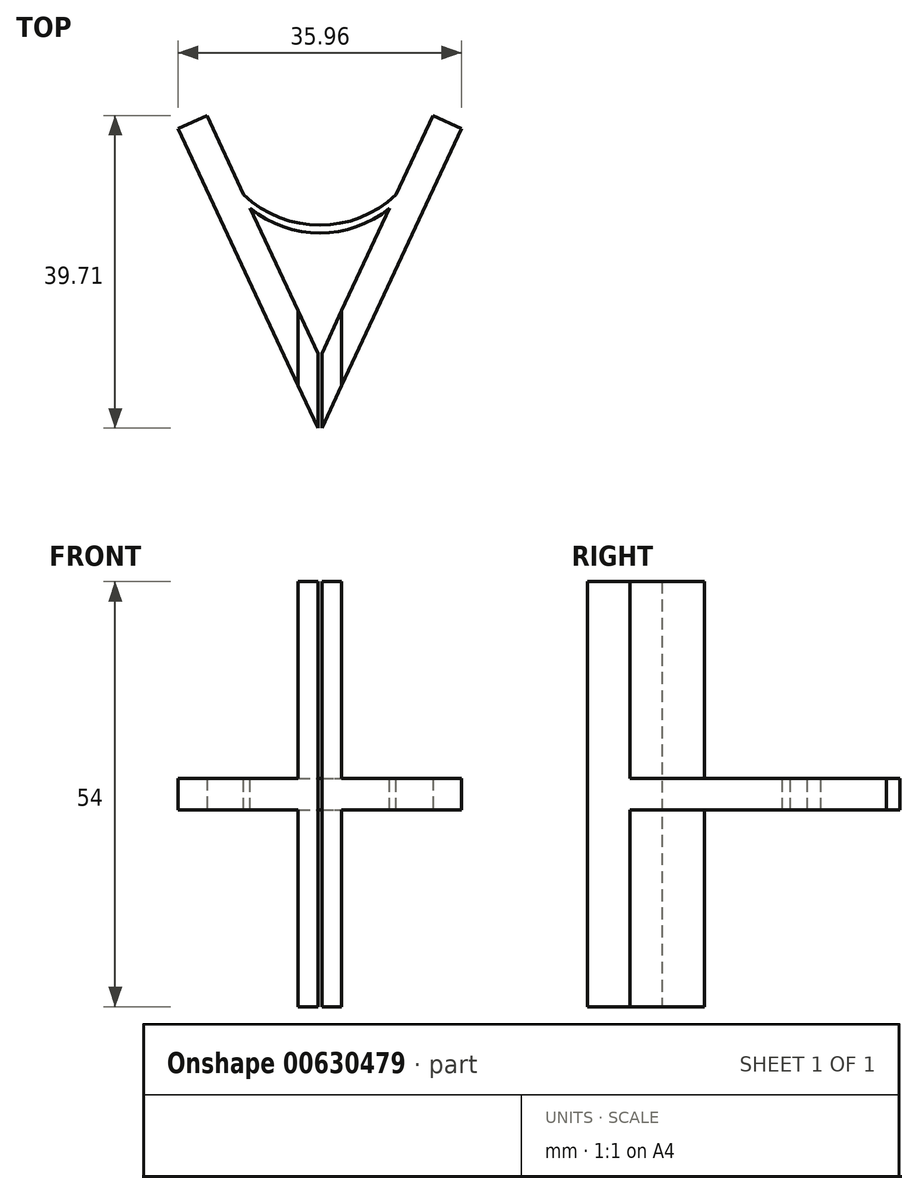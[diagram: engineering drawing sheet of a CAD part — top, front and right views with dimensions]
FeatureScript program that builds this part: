
annotation { "Feature Type Name" : "Feature", "Feature Type Description" : "" }
export const myFeature = defineFeature(function(context is Context, id is Id, definition is map)
    precondition{}
    {
        {
            var Q0;
            Q0=qCreatedBy(makeId("Top.planeOp"),FACE);
            var sketch = newSketch(context, id + "F0", { "sketchPlane" : qUnion([Q0])});
            skLineSegment(sketch, "E0", {"start": v(7.41, 0) * mm, "end": v(17.98, 22.66) * mm});
            skLineSegment(sketch, "E1", {"start": v(-7.41, 0) * mm, "end": v(-17.98, 22.66) * mm});
            skLineSegment(sketch, "E2", {"start": v(-17.98, 22.66) * mm, "end": v(-14.35, 24.35) * mm});
            skLineSegment(sketch, "E3", {"start": v(-14.35, 24.35) * mm, "end": v(-3, 0) * mm});
            skLineSegment(sketch, "E4", {"start": v(17.98, 22.66) * mm, "end": v(14.35, 24.35) * mm});
            skLineSegment(sketch, "E5", {"start": v(14.35, 24.35) * mm, "end": v(3, 0) * mm});
            skLineSegment(sketch, "E6", {"start": v(7.41, 0) * mm, "end": v(0, -15.9) * mm});
            skLineSegment(sketch, "E7", {"start": v(0, -15.9) * mm, "end": v(-7.41, 0) * mm});
            skLineSegment(sketch, "E8", {"start": v(-3, 0) * mm, "end": v(0, -6.43) * mm});
            skLineSegment(sketch, "E9", {"start": v(0, -6.43) * mm, "end": v(3, 0) * mm});
            skLineSegment(sketch, "E10", {"start": v(-0.25, -5.1) * mm, "end": v(0.25, -5.1) * mm});
            skLineSegment(sketch, "E11", {"start": v(0.25, -5.1) * mm, "end": v(0.25, -16.9) * mm});
            skLineSegment(sketch, "E12", {"start": v(0.25, -16.9) * mm, "end": v(-0.25, -16.9) * mm});
            skLineSegment(sketch, "E13", {"start": v(-0.25, -16.9) * mm, "end": v(-0.25, -5.1) * mm});
            skSolve(sketch);
        }
        {
            var Q0;
            {var subQ1=sQuery(id+"F0.wireOp",EDGE,"E1");Q0=makeQuery(id+"F0.imprint","IMPRINT",FACE,{"disambiguationData":[TD([[makeQuery(id+"F0.imprint","IMPRINT",EDGE,{"derivedFrom":subQ1}),-1.0]])]});}
            var Q1;
            {var subQ1=sQuery(id+"F0.wireOp",EDGE,"E0");Q1=makeQuery(id+"F0.imprint","IMPRINT",FACE,{"disambiguationData":[TD([[makeQuery(id+"F0.imprint","IMPRINT",EDGE,{"derivedFrom":subQ1}),1.0]])]});}
            var Q2;
            {var subQ5=sQuery(id+"F0.wireOp",EDGE,"E7");var subQ6=sQuery(id+"F0.wireOp",EDGE,"E6");var subQ7=makeQuery(id+"F0.imprint","INTERSECT",VERTEX,{"derivedFrom":[subQ6,subQ5]});Q2=makeQuery(id+"F0.imprint","IMPRINT",FACE,{"disambiguationData":[TD([[makeQuery(id+"F0.imprint","IMPRINT",EDGE,{"disambiguationData":[TD([[subQ7,1.0]])],"derivedFrom":subQ6}),-1.0]])]});}
            extrude(context, id + "F1", {"entities" : qUnion([Q0, Q1, Q2]), "depth" : 2 * mm, "offsetDistance" : 25 * mm});
        }
        {
            var Q0;
            Q0=makeQuery(id+"F1.opExtrude","CAP_FACE",FACE,{"disambiguationData":[OSD([sQuery(id+"F0.wireOp",EDGE,"E0"),sQuery(id+"F0.wireOp",EDGE,"E4"),sQuery(id+"F0.wireOp",EDGE,"E5"),sQuery(id+"F0.wireOp",EDGE,"E6"),sQuery(id+"F0.wireOp",EDGE,"E9"),sQuery(id+"F0.wireOp",EDGE,"E11")])],"isStart":false});
            var sketch = newSketch(context, id + "F2", { "sketchPlane" : qUnion([Q0])});
            skCircle(sketch, "E14", {"center": v(0, 23.42) * mm, "radius": 14 * mm});
            skCircle(sketch, "E15", {"center": v(0, 24.42) * mm, "radius": 14 * mm});
            skSolve(sketch);
        }
        {
            var Q0;
            {var subQ0=sQuery(id+"F2.wireOp",EDGE,"E14");var subQ1=makeQuery(id+"F1.opExtrude","CAP_EDGE",EDGE,{"disambiguationData":[OSD([sQuery(id+"F0.wireOp",EDGE,"E3"),sQuery(id+"F0.wireOp",EDGE,"E8")])],"isStart":false});var subQ2=makeQuery(id+"F2.imprint","INTERSECT",VERTEX,{"disambiguationData":[OD(1.0)],"derivedFrom":[subQ1,subQ0]});Q0=makeQuery(id+"F2.imprint","IMPRINT",FACE,{"disambiguationData":[TD([[makeQuery(id+"F2.imprint","IMPRINT",EDGE,{"disambiguationData":[TD([[subQ2,-1.0]])],"derivedFrom":subQ0}),1.0]])]});}
            extrude(context, id + "F3", {"entities" : qUnion([Q0]), "operationType" : NewBodyOperationType.ADD, "oppositeDirection" : true, "depth" : 4 * mm, "offsetDistance" : 25 * mm});
        }
        {
            var Q0;
            {var subQ0=sQuery(id+"F0.wireOp",EDGE,"E9");var subQ1=sQuery(id+"F0.wireOp",EDGE,"E8");var subQ2=sQuery(id+"F0.wireOp",EDGE,"E5");var subQ3=sQuery(id+"F0.wireOp",EDGE,"E3");Q0=makeQuery(id+"F3.boolean.opBoolean","MERGE",FACE,{"derivedFrom":[makeQuery(id+"F1.opExtrude","CAP_FACE",FACE,{"disambiguationData":[OSD([sQuery(id+"F0.wireOp",EDGE,"E0"),sQuery(id+"F0.wireOp",EDGE,"E1"),sQuery(id+"F0.wireOp",EDGE,"E2"),subQ3,sQuery(id+"F0.wireOp",EDGE,"E4"),subQ2,sQuery(id+"F0.wireOp",EDGE,"E6"),sQuery(id+"F0.wireOp",EDGE,"E7"),subQ1,subQ0])],"isStart":false}),makeQuery(id+"F3.opExtrude","CAP_FACE",FACE,{"disambiguationData":[OSD([subQ3,subQ2,subQ1,subQ0,sQuery(id+"F2.wireOp",EDGE,"E14"),sQuery(id+"F2.wireOp",EDGE,"E15")])],"isStart":true})]});}
            var sketch = newSketch(context, id + "F4", { "sketchPlane" : qUnion([Q0])});
            skLineSegment(sketch, "E16", {"start": v(-0.25, -1.87) * mm, "end": v(0.25, -1.87) * mm});
            skLineSegment(sketch, "E17", {"start": v(0.25, -1.87) * mm, "end": v(0.25, -16.87) * mm});
            skLineSegment(sketch, "E18", {"start": v(0.25, -16.87) * mm, "end": v(-0.25, -16.87) * mm});
            skLineSegment(sketch, "E19", {"start": v(-0.25, -16.87) * mm, "end": v(-0.25, -1.87) * mm});
            skSolve(sketch);
        }
        {
            var Q0;
            Q0 = qSketchRegion(id + "F4", true);
            extrude(context, id + "F5", {"entities" : qUnion([Q0]), "operationType" : NewBodyOperationType.REMOVE, "oppositeDirection" : true, "depth" : 25 * mm, "offsetDistance" : 25 * mm});
        }
        {
            var Q0;
            {var subQ0=sQuery(id+"F0.wireOp",EDGE,"E8");var subQ1=sQuery(id+"F0.wireOp",EDGE,"E3");var subQ2=sQuery(id+"F0.wireOp",EDGE,"E2");var subQ3=sQuery(id+"F0.wireOp",EDGE,"E7");var subQ4=sQuery(id+"F0.wireOp",EDGE,"E1");Q0=makeQuery(id+"F5.boolean.opBoolean","SPLIT",FACE,{"disambiguationData":[TD([makeQuery(id+"F1.opExtrude","SWEPT_FACE",FACE,{"disambiguationData":[OSD([subQ2])]})])],"derivedFrom":makeQuery(id+"F1.opExtrude","CAP_FACE",FACE,{"disambiguationData":[OSD([sQuery(id+"F0.wireOp",EDGE,"E0"),subQ4,subQ2,subQ1,sQuery(id+"F0.wireOp",EDGE,"E4"),sQuery(id+"F0.wireOp",EDGE,"E5"),sQuery(id+"F0.wireOp",EDGE,"E6"),subQ3,subQ0,sQuery(id+"F0.wireOp",EDGE,"E9")])],"isStart":true})});}
            var Q1;
            {var subQ0=sQuery(id+"F0.wireOp",EDGE,"E4");var subQ1=sQuery(id+"F0.wireOp",EDGE,"E9");var subQ2=sQuery(id+"F0.wireOp",EDGE,"E5");var subQ3=sQuery(id+"F0.wireOp",EDGE,"E6");var subQ4=sQuery(id+"F0.wireOp",EDGE,"E0");Q1=makeQuery(id+"F5.boolean.opBoolean","SPLIT",FACE,{"disambiguationData":[TD([makeQuery(id+"F1.opExtrude","SWEPT_FACE",FACE,{"disambiguationData":[OSD([subQ0])]})])],"derivedFrom":makeQuery(id+"F1.opExtrude","CAP_FACE",FACE,{"disambiguationData":[OSD([subQ4,sQuery(id+"F0.wireOp",EDGE,"E1"),sQuery(id+"F0.wireOp",EDGE,"E2"),sQuery(id+"F0.wireOp",EDGE,"E3"),subQ0,subQ2,subQ3,sQuery(id+"F0.wireOp",EDGE,"E7"),sQuery(id+"F0.wireOp",EDGE,"E8"),subQ1])],"isStart":true})});}
            extrude(context, id + "F6", {"entities" : qUnion([Q0, Q1]), "operationType" : NewBodyOperationType.ADD, "depth" : 2 * mm, "offsetDistance" : 25 * mm});
        }
        {
            var Q0;
            {var subQ0=sQuery(id+"F0.wireOp",EDGE,"E9");var subQ1=sQuery(id+"F0.wireOp",EDGE,"E8");var subQ2=sQuery(id+"F0.wireOp",EDGE,"E5");var subQ3=sQuery(id+"F0.wireOp",EDGE,"E3");Q0=makeQuery(id+"F3.boolean.opBoolean","MERGE",FACE,{"derivedFrom":[makeQuery(id+"F1.opExtrude","CAP_FACE",FACE,{"disambiguationData":[OSD([sQuery(id+"F0.wireOp",EDGE,"E0"),sQuery(id+"F0.wireOp",EDGE,"E1"),sQuery(id+"F0.wireOp",EDGE,"E2"),subQ3,sQuery(id+"F0.wireOp",EDGE,"E4"),subQ2,sQuery(id+"F0.wireOp",EDGE,"E6"),sQuery(id+"F0.wireOp",EDGE,"E7"),subQ1,subQ0])],"isStart":false}),makeQuery(id+"F3.opExtrude","CAP_FACE",FACE,{"disambiguationData":[OSD([subQ3,subQ2,subQ1,subQ0,sQuery(id+"F2.wireOp",EDGE,"E14"),sQuery(id+"F2.wireOp",EDGE,"E15")])],"isStart":true})]});}
            var sketch = newSketch(context, id + "F7", { "sketchPlane" : qUnion([Q0])});
            skLineSegment(sketch, "E20", {"start": v(2.79, -0.46) * mm, "end": v(2.79, -9.92) * mm});
            skLineSegment(sketch, "E21", {"start": v(-2.79, -0.46) * mm, "end": v(-2.79, -9.92) * mm});
            skSolve(sketch);
        }
        {
            var Q0;
            Q0 = qSketchRegion(id + "F7", true);
            var Q1;
            {var subQ0=sQuery(id+"F7.wireOp",EDGE,"E21");Q1=makeQuery(id+"F7.imprint","IMPRINT",FACE,{"disambiguationData":[TD([[makeQuery(id+"F7.imprint","IMPRINT",EDGE,{"derivedFrom":subQ0}),1.0]])]});}
            var Q2;
            {var subQ0=sQuery(id+"F7.wireOp",EDGE,"E20");Q2=makeQuery(id+"F7.imprint","IMPRINT",FACE,{"disambiguationData":[TD([[makeQuery(id+"F7.imprint","IMPRINT",EDGE,{"derivedFrom":subQ0}),-1.0]])]});}
            extrude(context, id + "F8", {"entities" : qUnion([Q0, Q1, Q2]), "operationType" : NewBodyOperationType.ADD, "depth" : 25 * mm, "offsetDistance" : 25 * mm});
        }
        {
            var Q0;
            {var subQ0=sQuery(id+"F2.wireOp",EDGE,"E14");var subQ2=sQuery(id+"F0.wireOp",EDGE,"E4");var subQ3=sQuery(id+"F0.wireOp",EDGE,"E9");var subQ4=sQuery(id+"F0.wireOp",EDGE,"E5");var subQ5=sQuery(id+"F0.wireOp",EDGE,"E6");var subQ6=sQuery(id+"F0.wireOp",EDGE,"E0");var subQ7=sQuery(id+"F2.wireOp",EDGE,"E15");var subQ9=sQuery(id+"F0.wireOp",EDGE,"E8");var subQ10=sQuery(id+"F0.wireOp",EDGE,"E7");var subQ11=sQuery(id+"F0.wireOp",EDGE,"E3");var subQ12=sQuery(id+"F0.wireOp",EDGE,"E2");var subQ13=sQuery(id+"F0.wireOp",EDGE,"E1");var subQ14=makeQuery(id+"F1.opExtrude","CAP_FACE",FACE,{"disambiguationData":[OSD([subQ6,subQ13,subQ12,subQ11,subQ2,subQ4,subQ5,subQ10,subQ9,subQ3])],"isStart":true});Q0=makeQuery(id+"F6.boolean.opBoolean","MERGE",FACE,{"derivedFrom":[makeQuery(id+"F3.opExtrude","CAP_FACE",FACE,{"disambiguationData":[OSD([subQ11,subQ4,subQ9,subQ3,subQ0,subQ7])],"isStart":false}),makeQuery(id+"F6.opExtrude","CAP_FACE",FACE,{"disambiguationData":[OSD([subQ6,subQ13,subQ12,subQ11,subQ2,subQ4,subQ5,subQ10,subQ9,subQ3]),TDD([makeQuery(id+"F5.boolean.opBoolean","SPLIT",FACE,{"disambiguationData":[TD([makeQuery(id+"F1.opExtrude","SWEPT_FACE",FACE,{"disambiguationData":[OSD([subQ12])]})])],"derivedFrom":subQ14})])],"isStart":false}),makeQuery(id+"F6.opExtrude","CAP_FACE",FACE,{"disambiguationData":[OSD([subQ6,subQ13,subQ12,subQ11,subQ2,subQ4,subQ5,subQ10,subQ9,subQ3]),TDD([makeQuery(id+"F5.boolean.opBoolean","SPLIT",FACE,{"disambiguationData":[TD([makeQuery(id+"F1.opExtrude","SWEPT_FACE",FACE,{"disambiguationData":[OSD([subQ2])]})])],"derivedFrom":subQ14})])],"isStart":false})]});}
            var sketch = newSketch(context, id + "F9", { "sketchPlane" : qUnion([Q0])});
            skLineSegment(sketch, "E22", {"start": v(-2.79, 9.92) * mm, "end": v(-2.79, 0.46) * mm});
            skLineSegment(sketch, "E23", {"start": v(2.79, 0.46) * mm, "end": v(2.79, 9.92) * mm});
            skSolve(sketch);
        }
        {
            var Q0;
            Q0 = qSketchRegion(id + "F9", true);
            var Q1;
            {var subQ0=sQuery(id+"F9.wireOp",EDGE,"E22");Q1=makeQuery(id+"F9.imprint","IMPRINT",FACE,{"disambiguationData":[TD([[makeQuery(id+"F9.imprint","IMPRINT",EDGE,{"derivedFrom":subQ0}),1.0]])]});}
            var Q2;
            {var subQ0=sQuery(id+"F9.wireOp",EDGE,"E23");Q2=makeQuery(id+"F9.imprint","IMPRINT",FACE,{"disambiguationData":[TD([[makeQuery(id+"F9.imprint","IMPRINT",EDGE,{"derivedFrom":subQ0}),1.0]])]});}
            extrude(context, id + "F10", {"entities" : qUnion([Q0, Q1, Q2]), "operationType" : NewBodyOperationType.ADD, "depth" : 25 * mm, "offsetDistance" : 25 * mm});
        }
    });
